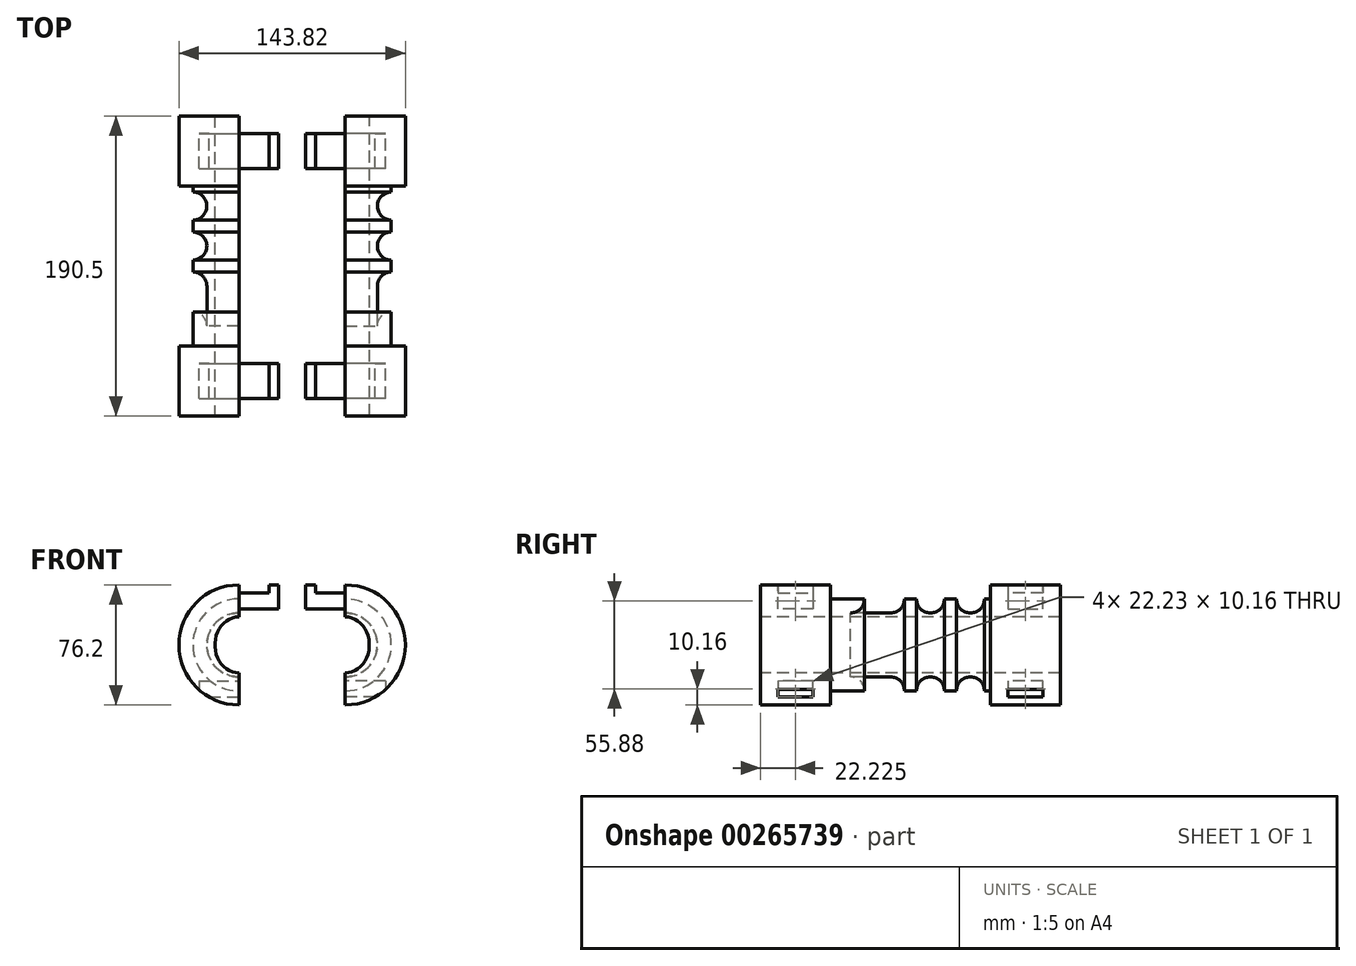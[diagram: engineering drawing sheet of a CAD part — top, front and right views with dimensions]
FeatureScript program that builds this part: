
annotation { "Feature Type Name" : "Feature", "Feature Type Description" : "" }
export const myFeature = defineFeature(function(context is Context, id is Id, definition is map)
    precondition{}
    {
        {
            var Q0;
            Q0=qCreatedBy(makeId("Top.planeOp"),FACE);
            var sketch = newSketch(context, id + "F0", { "sketchPlane" : qUnion([Q0])});
            skLineSegment(sketch, "E0.bottom", {"start": v(-71.9, 95.25) * mm, "end": v(-33.8, 95.25) * mm});
            skLineSegment(sketch, "E0.top", {"start": v(-71.9, -95.25) * mm, "end": v(-33.8, -95.25) * mm});
            skLineSegment(sketch, "E0.left", {"start": v(-71.9, 95.25) * mm, "end": v(-71.9, -95.25) * mm});
            skLineSegment(sketch, "E0.right", {"start": v(-33.8, 95.25) * mm, "end": v(-33.8, -95.25) * mm});
            skLineSegment(sketch, "E1", {"start": v(-99.1, -95.25) * mm, "end": v(-99.1, -50.8) * mm, "construction": true});
            skLineSegment(sketch, "E2", {"start": v(-99.1, 95.25) * mm, "end": v(-99.1, 50.8) * mm, "construction": true});
            skLineSegment(sketch, "E3", {"start": v(-71.9, -50.8) * mm, "end": v(-63.02, -50.8) * mm});
            skLineSegment(sketch, "E4", {"start": v(-63.02, 0) * mm, "end": v(-63.02, 50.8) * mm});
            skLineSegment(sketch, "E5", {"start": v(-63.02, 50.8) * mm, "end": v(-71.9, 50.8) * mm});
            skLineSegment(sketch, "E6", {"start": v(-63.02, 50.8) * mm, "end": v(-6.32, 50.8) * mm});
            skLineSegment(sketch, "E7", {"start": v(-6.32, 50.8) * mm, "end": v(-6.32, 0) * mm});
            skLineSegment(sketch, "E8", {"start": v(-63.02, 0) * mm, "end": v(-63.02, -50.8) * mm});
            skArc(sketch, "E9", {"start": v(-63.02, 29.2) * mm, "mid": v(-54.13, 38.1) * mm, "end": v(-63.02, 46.99) * mm});
            skArc(sketch, "E10", {"start": v(-63.02, 3.8) * mm, "mid": v(-54.13, 12.7) * mm, "end": v(-63.02, 21.59) * mm});
            skArc(sketch, "E11", {"start": v(-63.02, -47) * mm, "mid": v(-54.13, -38.1) * mm, "end": v(-63.02, -29.21) * mm});
            skArc(sketch, "E12", {"start": v(-63.02, -21.6) * mm, "mid": v(-54.13, -12.7) * mm, "end": v(-63.02, -3.81) * mm});
            skPoint(sketch, "E13.end.orphan", {"position": v(-71.9, 0) * mm});
            skLineSegment(sketch, "E14", {"start": v(-54.13, 50.8) * mm, "end": v(-54.13, -50.8) * mm});
            skPoint(sketch, "E14.startSnap0", {"position": v(-54.13, 38.1) * mm});
            skLineSegment(sketch, "E15", {"start": v(-54.13, -50.8) * mm, "end": v(-63.02, -50.8) * mm});
            skSolve(sketch);
        }
        {
            var Q0;
            {var subQ2=sQuery(id+"F0.wireOp",EDGE,"E0.bottom");Q0=makeQuery(id+"F0.imprint","IMPRINT",FACE,{"disambiguationData":[TD([[makeQuery(id+"F0.imprint","IMPRINT",EDGE,{"derivedFrom":subQ2}),-1.0]])]});}
            var Q1;
            {var subQ10=sQuery(id+"F0.wireOp",EDGE,"E0.top");Q1=makeQuery(id+"F0.imprint","IMPRINT",FACE,{"disambiguationData":[TD([[makeQuery(id+"F0.imprint","IMPRINT",EDGE,{"derivedFrom":subQ10}),1.0]])]});}
            var Q2;
            {var subQ1=sQuery(id+"F0.wireOp",EDGE,"E4");var subQ3=sQuery(id+"F0.wireOp",EDGE,"E9");var subQ4=makeQuery(id+"F0.imprint","INTERSECT",VERTEX,{"disambiguationData":[OD(1.0)],"derivedFrom":[subQ1,subQ3]});Q2=makeQuery(id+"F0.imprint","IMPRINT",FACE,{"disambiguationData":[TD([[makeQuery(id+"F0.imprint","IMPRINT",EDGE,{"disambiguationData":[TD([[subQ4,1.0]])],"derivedFrom":subQ3}),-1.0]])]});}
            var Q3;
            {var subQ0=sQuery(id+"F0.wireOp",EDGE,"E9");var subQ1=sQuery(id+"F0.wireOp",EDGE,"E4");var subQ2=makeQuery(id+"F0.imprint","INTERSECT",VERTEX,{"disambiguationData":[OD(0.0)],"derivedFrom":[subQ1,subQ0]});Q3=makeQuery(id+"F0.imprint","IMPRINT",FACE,{"disambiguationData":[TD([[makeQuery(id+"F0.imprint","IMPRINT",EDGE,{"disambiguationData":[TD([[subQ2,1.0]])],"derivedFrom":subQ1}),-1.0]])]});}
            var Q4;
            {var subQ0=sQuery(id+"F0.wireOp",EDGE,"E8");var subQ1=sQuery(id+"F0.wireOp",EDGE,"E4");var subQ2=makeQuery(id+"F0.imprint","INTERSECT",VERTEX,{"derivedFrom":[subQ1,subQ0]});Q4=makeQuery(id+"F0.imprint","IMPRINT",FACE,{"disambiguationData":[TD([[makeQuery(id+"F0.imprint","IMPRINT",EDGE,{"disambiguationData":[TD([[subQ2,-1.0]])],"derivedFrom":subQ1}),-1.0]])]});}
            var Q5;
            {var subQ0=sQuery(id+"F0.wireOp",EDGE,"E11");var subQ1=sQuery(id+"F0.wireOp",EDGE,"E8");var subQ2=makeQuery(id+"F0.imprint","INTERSECT",VERTEX,{"disambiguationData":[OD(1.0)],"derivedFrom":[subQ1,subQ0]});Q5=makeQuery(id+"F0.imprint","IMPRINT",FACE,{"disambiguationData":[TD([[makeQuery(id+"F0.imprint","IMPRINT",EDGE,{"disambiguationData":[TD([[subQ2,1.0]])],"derivedFrom":subQ1}),1.0]])]});}
            var Q6;
            {var subQ0=sQuery(id+"F0.wireOp",EDGE,"E15");Q6=makeQuery(id+"F0.imprint","IMPRINT",FACE,{"disambiguationData":[TD([[makeQuery(id+"F0.imprint","IMPRINT",EDGE,{"derivedFrom":subQ0}),-1.0]])]});}
            var Q7;
            Q7=sQuery(id+"F0.wireOp",EDGE,"E0.right");
            revolve(context, id + "F1", {"entities" : qUnion([Q0, Q1, Q2, Q3, Q4, Q5, Q6]), "axis" : qUnion([Q7]), "revolveType" : RevolveType.SYMMETRIC, "angle" : 180 * degree});
        }
        {
            var Q0;
            Q0=makeQuery(id+"F1.opRevolve","SWEPT_FACE",FACE,{"disambiguationData":[OSD([sQuery(id+"F0.wireOp",EDGE,"E0.top")])]});
            var sketch = newSketch(context, id + "F2", { "sketchPlane" : qUnion([Q0])});
            skEllipse(sketch, "E16", {"center": v(-33.8, 0) * mm, "majorRadius": 15.24 * mm, "minorRadius": 17.78 * mm, "majorAxis": v(-1, 0)});
            skSolve(sketch);
        }
        {
            var Q0;
            {var subQ0=sQuery(id+"F2.wireOp",EDGE,"YliuBiGO-nQju-PTa7-kItf-F8T7jNwYJWdv");var subQ1=makeQuery(id+"F1.opRevolve","CAP_EDGE",EDGE,{"disambiguationData":[OSD([sQuery(id+"F0.wireOp",EDGE,"E0.top")])],"isStart":true});var subQ2=makeQuery(id+"F2.imprint","INTERSECT",VERTEX,{"disambiguationData":[OD(0.0)],"derivedFrom":[subQ1,subQ0]});Q0=makeQuery(id+"F2.imprint","IMPRINT",FACE,{"disambiguationData":[TD([[makeQuery(id+"F2.imprint","IMPRINT",EDGE,{"disambiguationData":[TD([[subQ2,-1.0]])],"derivedFrom":subQ0}),1.0]])]});}
            var Q1;
            {var subQ0=sQuery(id+"F2.wireOp",EDGE,"E16");var subQ1=makeQuery(id+"F1.opRevolve","CAP_EDGE",EDGE,{"disambiguationData":[OSD([sQuery(id+"F0.wireOp",EDGE,"E0.top")])],"isStart":false});var subQ2=makeQuery(id+"F2.imprint","INTERSECT",VERTEX,{"disambiguationData":[OD(0.0)],"derivedFrom":[subQ1,subQ0]});Q1=makeQuery(id+"F2.imprint","IMPRINT",FACE,{"disambiguationData":[TD([[makeQuery(id+"F2.imprint","IMPRINT",EDGE,{"disambiguationData":[TD([[subQ2,-1.0]])],"derivedFrom":subQ0}),1.0]])]});}
            extrude(context, id + "F3", {"entities" : qUnion([Q0, Q1]), "operationType" : NewBodyOperationType.REMOVE, "oppositeDirection" : true, "depth" : 190.5 * mm});
        }
        {
            var Q0;
            Q0=makeQuery(id+"F3.boolean.opBoolean","SPLIT",FACE,{"disambiguationData":[OD(1.0)],"derivedFrom":makeQuery(id+"F1.opRevolve","CAP_FACE",FACE,{"disambiguationData":[OSD([sQuery(id+"F0.wireOp",EDGE,"E0.bottom"),sQuery(id+"F0.wireOp",EDGE,"E0.top"),sQuery(id+"F0.wireOp",EDGE,"E0.left"),sQuery(id+"F0.wireOp",EDGE,"E0.right"),sQuery(id+"F0.wireOp",EDGE,"E3"),sQuery(id+"F0.wireOp",EDGE,"E4"),sQuery(id+"F0.wireOp",EDGE,"E5"),sQuery(id+"F0.wireOp",EDGE,"E8"),sQuery(id+"F0.wireOp",EDGE,"E9"),sQuery(id+"F0.wireOp",EDGE,"E10"),sQuery(id+"F0.wireOp",EDGE,"E11"),sQuery(id+"F0.wireOp",EDGE,"E12")])],"isStart":false})});
            var sketch = newSketch(context, id + "F4", { "sketchPlane" : qUnion([Q0])});
            skLineSegment(sketch, "E17", {"start": v(-50.8, -29.21) * mm, "end": v(-50.8, -17.78) * mm});
            skLineSegment(sketch, "E18", {"start": v(-95.25, -27.94) * mm, "end": v(-73.03, -27.94) * mm});
            skLineSegment(sketch, "E19", {"start": v(-84.14, -27.94) * mm, "end": v(-84.14, -33.02) * mm});
            skLineSegment(sketch, "E20", {"start": v(-84.14, -33.02) * mm, "end": v(-61.91, -33.02) * mm});
            skLineSegment(sketch, "E21", {"start": v(-61.91, -33.02) * mm, "end": v(-61.91, -22.86) * mm});
            skLineSegment(sketch, "E22", {"start": v(-61.91, -22.86) * mm, "end": v(-84.14, -22.86) * mm});
            skLineSegment(sketch, "E23", {"start": v(-84.14, -22.86) * mm, "end": v(-84.14, -27.94) * mm});
            skSolve(sketch);
        }
        {
            var Q0;
            Q0=makeQuery(id+"F4.imprint","IMPRINT",FACE,{"disambiguationData":[TD([[makeQuery(id+"F4.imprint","IMPRINT",EDGE,{"derivedFrom":sQuery(id+"F4.wireOp",EDGE,"E19")}),1.0]])]});
            extrude(context, id + "F5", {"entities" : qUnion([Q0]), "operationType" : NewBodyOperationType.REMOVE, "oppositeDirection" : true, "depth" : 25.4 * mm});
        }
        {
            var Q0;
            Q0=makeQuery(id+"F3.boolean.opBoolean","SPLIT",FACE,{"disambiguationData":[OD(1.0)],"derivedFrom":makeQuery(id+"F1.opRevolve","CAP_FACE",FACE,{"disambiguationData":[OSD([sQuery(id+"F0.wireOp",EDGE,"E0.bottom"),sQuery(id+"F0.wireOp",EDGE,"E0.top"),sQuery(id+"F0.wireOp",EDGE,"E0.left"),sQuery(id+"F0.wireOp",EDGE,"E0.right"),sQuery(id+"F0.wireOp",EDGE,"E3"),sQuery(id+"F0.wireOp",EDGE,"E4"),sQuery(id+"F0.wireOp",EDGE,"E5"),sQuery(id+"F0.wireOp",EDGE,"E8"),sQuery(id+"F0.wireOp",EDGE,"E9"),sQuery(id+"F0.wireOp",EDGE,"E10"),sQuery(id+"F0.wireOp",EDGE,"E11"),sQuery(id+"F0.wireOp",EDGE,"E12")])],"isStart":false})});
            var sketch = newSketch(context, id + "F6", { "sketchPlane" : qUnion([Q0])});
            skLineSegment(sketch, "E24", {"start": v(50.8, -29.21) * mm, "end": v(50.8, -17.78) * mm});
            skLineSegment(sketch, "E25", {"start": v(95.25, -27.94) * mm, "end": v(73.03, -27.94) * mm});
            skPoint(sketch, "E25.endSnap0", {"position": v(95.25, -27.94) * mm});
            skLineSegment(sketch, "E26", {"start": v(84.14, -27.94) * mm, "end": v(84.14, -22.86) * mm});
            skPoint(sketch, "E26.endSnap0", {"position": v(84.14, -27.94) * mm});
            skLineSegment(sketch, "E27", {"start": v(84.14, -22.86) * mm, "end": v(61.91, -22.86) * mm});
            skLineSegment(sketch, "E28", {"start": v(61.91, -22.86) * mm, "end": v(61.91, -33.02) * mm});
            skLineSegment(sketch, "E29", {"start": v(61.91, -33.02) * mm, "end": v(84.14, -33.02) * mm});
            skLineSegment(sketch, "E30", {"start": v(84.14, -33.02) * mm, "end": v(84.14, -27.94) * mm});
            skSolve(sketch);
        }
        {
            var Q0;
            Q0=makeQuery(id+"F6.imprint","IMPRINT",FACE,{"disambiguationData":[TD([[makeQuery(id+"F6.imprint","IMPRINT",EDGE,{"derivedFrom":sQuery(id+"F6.wireOp",EDGE,"E26")}),1.0]])]});
            extrude(context, id + "F7", {"entities" : qUnion([Q0]), "operationType" : NewBodyOperationType.REMOVE, "oppositeDirection" : true, "depth" : 25.4 * mm});
        }
        {
            var Q0;
            Q0=makeQuery(id+"F3.boolean.opBoolean","SPLIT",FACE,{"disambiguationData":[OD(0.0)],"derivedFrom":makeQuery(id+"F1.opRevolve","CAP_FACE",FACE,{"disambiguationData":[OSD([sQuery(id+"F0.wireOp",EDGE,"E0.bottom"),sQuery(id+"F0.wireOp",EDGE,"E0.top"),sQuery(id+"F0.wireOp",EDGE,"E0.left"),sQuery(id+"F0.wireOp",EDGE,"E0.right"),sQuery(id+"F0.wireOp",EDGE,"E3"),sQuery(id+"F0.wireOp",EDGE,"E4"),sQuery(id+"F0.wireOp",EDGE,"E5"),sQuery(id+"F0.wireOp",EDGE,"E8"),sQuery(id+"F0.wireOp",EDGE,"E9"),sQuery(id+"F0.wireOp",EDGE,"E10"),sQuery(id+"F0.wireOp",EDGE,"E11"),sQuery(id+"F0.wireOp",EDGE,"E12")])],"isStart":false})});
            var sketch = newSketch(context, id + "F8", { "sketchPlane" : qUnion([Q0])});
            skLineSegment(sketch, "E31", {"start": v(-50.8, 29.21) * mm, "end": v(-50.8, 17.78) * mm});
            skLineSegment(sketch, "E32", {"start": v(-95.25, 27.94) * mm, "end": v(-73.03, 27.94) * mm});
            skLineSegment(sketch, "E33", {"start": v(-84.14, 27.94) * mm, "end": v(-84.14, 33.02) * mm});
            skLineSegment(sketch, "E34", {"start": v(-84.14, 33.02) * mm, "end": v(-61.91, 33.02) * mm});
            skLineSegment(sketch, "E35", {"start": v(-61.91, 33.02) * mm, "end": v(-61.91, 22.86) * mm});
            skLineSegment(sketch, "E36", {"start": v(-61.91, 22.86) * mm, "end": v(-84.14, 22.86) * mm});
            skLineSegment(sketch, "E37", {"start": v(-84.14, 22.86) * mm, "end": v(-84.14, 27.94) * mm});
            skSolve(sketch);
        }
        {
            var Q0;
            Q0=makeQuery(id+"F8.imprint","IMPRINT",FACE,{"disambiguationData":[TD([[makeQuery(id+"F8.imprint","IMPRINT",EDGE,{"derivedFrom":sQuery(id+"F8.wireOp",EDGE,"E33")}),-1.0]])]});
            extrude(context, id + "F9", {"entities" : qUnion([Q0]), "operationType" : NewBodyOperationType.ADD, "depth" : 25.4 * mm});
        }
        {
            var Q0;
            Q0=makeQuery(id+"F3.boolean.opBoolean","SPLIT",FACE,{"disambiguationData":[OD(0.0)],"derivedFrom":makeQuery(id+"F1.opRevolve","CAP_FACE",FACE,{"disambiguationData":[OSD([sQuery(id+"F0.wireOp",EDGE,"E0.bottom"),sQuery(id+"F0.wireOp",EDGE,"E0.top"),sQuery(id+"F0.wireOp",EDGE,"E0.left"),sQuery(id+"F0.wireOp",EDGE,"E0.right"),sQuery(id+"F0.wireOp",EDGE,"E3"),sQuery(id+"F0.wireOp",EDGE,"E4"),sQuery(id+"F0.wireOp",EDGE,"E5"),sQuery(id+"F0.wireOp",EDGE,"E8"),sQuery(id+"F0.wireOp",EDGE,"E9"),sQuery(id+"F0.wireOp",EDGE,"E10"),sQuery(id+"F0.wireOp",EDGE,"E11"),sQuery(id+"F0.wireOp",EDGE,"E12")])],"isStart":false})});
            var sketch = newSketch(context, id + "F10", { "sketchPlane" : qUnion([Q0])});
            skLineSegment(sketch, "E38", {"start": v(50.8, 29.2) * mm, "end": v(50.8, 17.78) * mm});
            skLineSegment(sketch, "E39", {"start": v(95.25, 27.94) * mm, "end": v(73.03, 27.94) * mm});
            skPoint(sketch, "E39.endSnap0", {"position": v(95.25, 27.94) * mm});
            skLineSegment(sketch, "E40", {"start": v(84.14, 27.94) * mm, "end": v(84.14, 33.02) * mm});
            skLineSegment(sketch, "E41", {"start": v(84.14, 33.02) * mm, "end": v(61.91, 33.02) * mm});
            skLineSegment(sketch, "E42", {"start": v(61.91, 33.02) * mm, "end": v(61.91, 22.86) * mm});
            skLineSegment(sketch, "E43", {"start": v(61.91, 22.86) * mm, "end": v(84.14, 22.86) * mm});
            skLineSegment(sketch, "E44", {"start": v(84.14, 22.86) * mm, "end": v(84.14, 27.94) * mm});
            skSolve(sketch);
        }
        {
            var Q0;
            Q0=makeQuery(id+"F10.imprint","IMPRINT",FACE,{"disambiguationData":[TD([[makeQuery(id+"F10.imprint","IMPRINT",EDGE,{"derivedFrom":sQuery(id+"F10.wireOp",EDGE,"E40")}),1.0]])]});
            extrude(context, id + "F11", {"entities" : qUnion([Q0]), "operationType" : NewBodyOperationType.ADD, "depth" : 25.4 * mm});
        }
        {
            var Q0;
            Q0=makeQuery(id+"F11.opExtrude","SWEPT_FACE",FACE,{"disambiguationData":[OSD([sQuery(id+"F10.wireOp",EDGE,"E43")])]});
            var sketch = newSketch(context, id + "F12", { "sketchPlane" : qUnion([Q0])});
            skLineSegment(sketch, "E45", {"start": v(-14.76, -84.14) * mm, "end": v(-14.76, -61.91) * mm});
            skSolve(sketch);
        }
        {
            var Q0;
            Q0=makeQuery(id+"F9.opExtrude","SWEPT_FACE",FACE,{"disambiguationData":[OSD([sQuery(id+"F8.wireOp",EDGE,"E36")])]});
            var sketch = newSketch(context, id + "F13", { "sketchPlane" : qUnion([Q0])});
            skLineSegment(sketch, "E46", {"start": v(-14.76, 61.91) * mm, "end": v(-14.76, 84.14) * mm});
            skSolve(sketch);
        }
        {
            var Q0;
            {var subQ0=sQuery(id+"F13.wireOp",EDGE,"E46");Q0=makeQuery(id+"F13.imprint","IMPRINT",FACE,{"disambiguationData":[TD([[makeQuery(id+"F13.imprint","IMPRINT",EDGE,{"derivedFrom":subQ0}),-1.0]])]});}
            var Q1;
            {var subQ0=sQuery(id+"F12.wireOp",EDGE,"E45");Q1=makeQuery(id+"F12.imprint","IMPRINT",FACE,{"disambiguationData":[TD([[makeQuery(id+"F12.imprint","IMPRINT",EDGE,{"derivedFrom":subQ0}),-1.0]])]});}
            extrude(context, id + "F14", {"entities" : qUnion([Q0, Q1]), "operationType" : NewBodyOperationType.ADD, "oppositeDirection" : true, "depth" : 15.24 * mm});
        }
        {
            var Q0;
            Q0=makeQuery(id+"F1.opRevolve","SWEPT_BODY",BODY,{"disambiguationData":[OSD([sQuery(id+"F0.wireOp",EDGE,"E0.bottom"),sQuery(id+"F0.wireOp",EDGE,"E0.top"),sQuery(id+"F0.wireOp",EDGE,"E0.left"),sQuery(id+"F0.wireOp",EDGE,"E0.right"),sQuery(id+"F0.wireOp",EDGE,"E3"),sQuery(id+"F0.wireOp",EDGE,"E5"),sQuery(id+"F0.wireOp",EDGE,"E6"),sQuery(id+"F0.wireOp",EDGE,"E14"),sQuery(id+"F0.wireOp",EDGE,"E15")])]});
            var Q1;
            Q1=qCreatedBy(makeId("Right.planeOp"),FACE);
            mirror(context, id + "F15", {"entities" : qUnion([Q0]), "mirrorPlane" : qUnion([Q1])});
        }
    });
